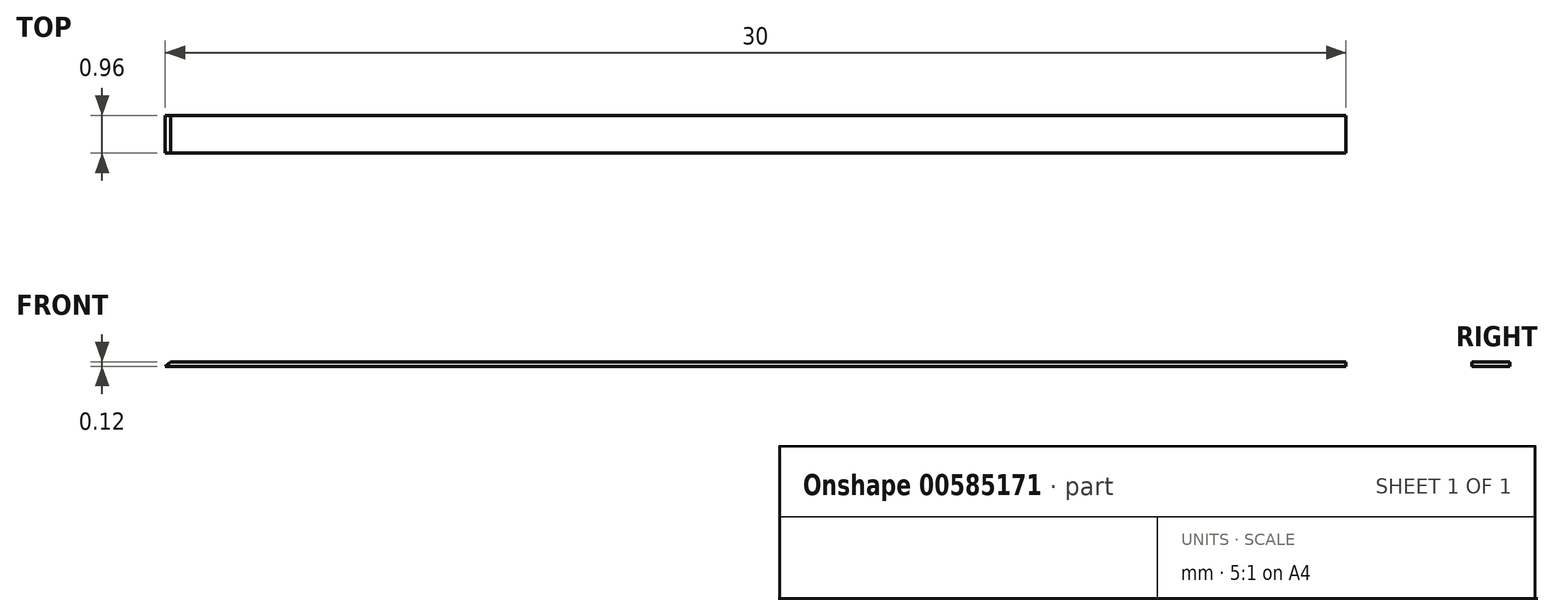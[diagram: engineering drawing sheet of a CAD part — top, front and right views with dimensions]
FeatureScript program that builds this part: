
annotation { "Feature Type Name" : "Feature", "Feature Type Description" : "" }
export const myFeature = defineFeature(function(context is Context, id is Id, definition is map)
    precondition{}
    {
        {
            var Q0;
            Q0=qCreatedBy(makeId("Front.planeOp"),FACE);
            var sketch = newSketch(context, id + "F0", { "sketchPlane" : qUnion([Q0])});
            skLineSegment(sketch, "E0.bottom", {"start": v(0, 0) * mm, "end": v(-30, 0) * mm});
            skLineSegment(sketch, "E0.top", {"start": v(0, 0.12) * mm, "end": v(-29.87, 0.12) * mm});
            skLineSegment(sketch, "E0.left", {"start": v(0, 0) * mm, "end": v(0, 0.12) * mm});
            skLineSegment(sketch, "E1", {"start": v(-30, 0) * mm, "end": v(-29.87, 0.12) * mm});
            skSolve(sketch);
        }
        {
            var Q0;
            Q0 = qSketchRegion(id + "F0", true);
            extrude(context, id + "F1", {"entities" : qUnion([Q0]), "depth" : 0.96 * mm, "offsetDistance" : 25 * mm});
        }
    });
